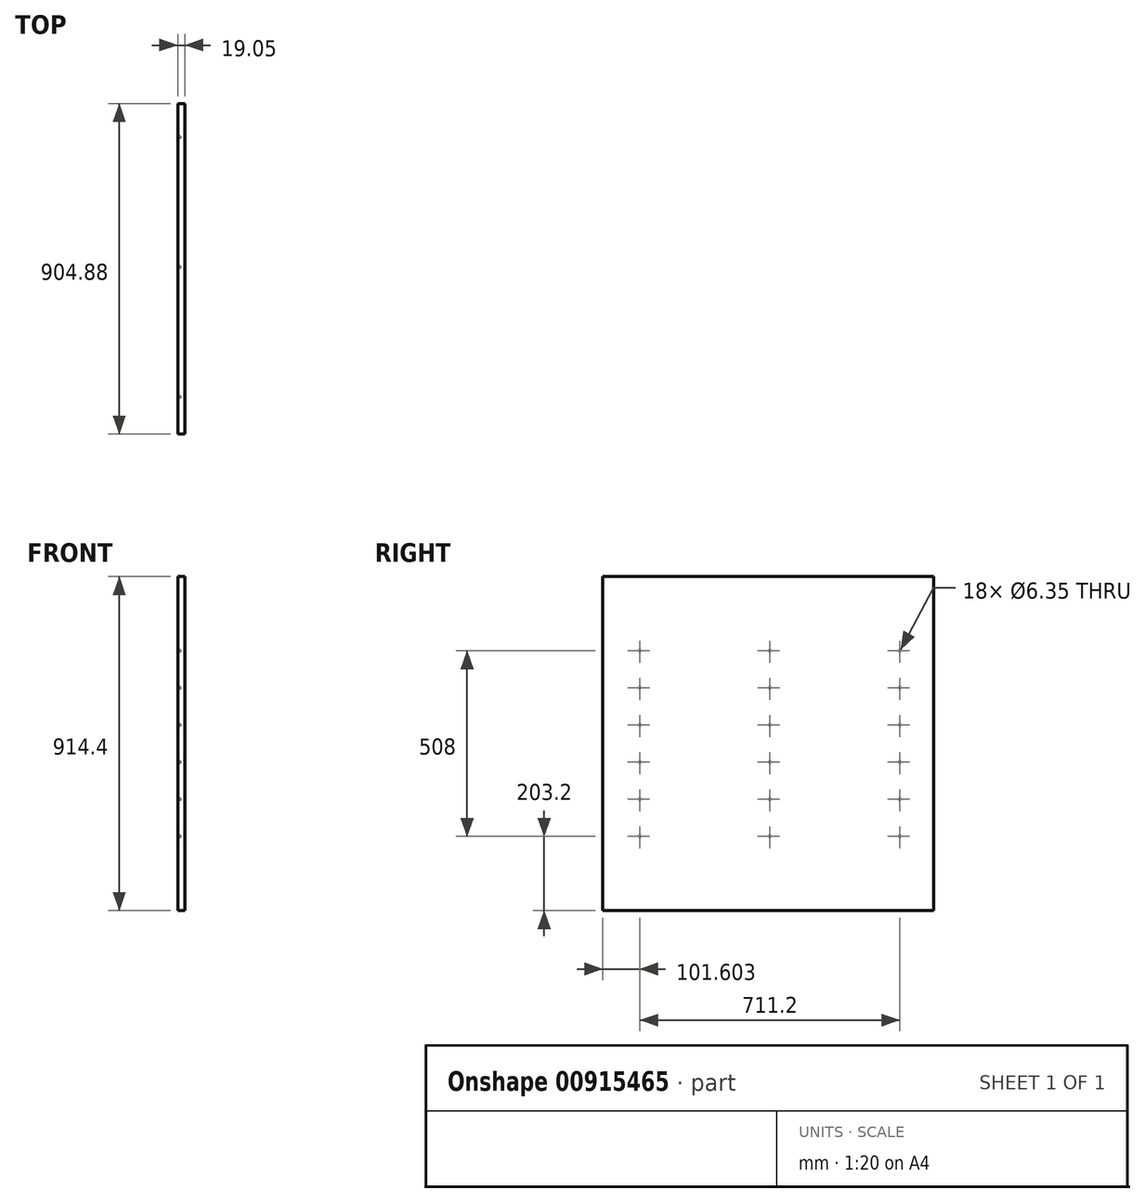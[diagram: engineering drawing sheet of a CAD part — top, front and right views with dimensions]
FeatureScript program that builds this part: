
annotation { "Feature Type Name" : "Feature", "Feature Type Description" : "" }
export const myFeature = defineFeature(function(context is Context, id is Id, definition is map)
    precondition{}
    {
        {
            var Q0;
            Q0=qCreatedBy(makeId("Right.planeOp"),FACE);
            var sketch = newSketch(context, id + "F0", { "sketchPlane" : qUnion([Q0])});
            skLineSegment(sketch, "E0.bottom", {"start": v(452.44, 457.2) * mm, "end": v(-452.44, 457.2) * mm});
            skLineSegment(sketch, "E0.top", {"start": v(452.44, -457.2) * mm, "end": v(-452.44, -457.2) * mm});
            skLineSegment(sketch, "E0.left", {"start": v(452.44, 457.2) * mm, "end": v(452.44, -457.2) * mm});
            skLineSegment(sketch, "E0.right", {"start": v(-452.44, 457.2) * mm, "end": v(-452.44, -457.2) * mm});
            skPoint(sketch, "E0.middle", {"position": v(0, 0) * mm});
            skSolve(sketch);
        }
        {
            var Q0;
            Q0=makeQuery(id+"F0.imprint","IMPRINT",FACE,{"disambiguationData":[TD([[makeQuery(id+"F0.imprint","IMPRINT",EDGE,{"derivedFrom":sQuery(id+"F0.wireOp",EDGE,"E0.bottom")}),1.0]])]});
            extrude(context, id + "F1", {"entities" : qUnion([Q0]), "depth" : 19.05 * mm, "offsetDistance" : 25.4 * mm});
        }
        {
            var Q0;
            Q0=makeQuery(id+"F1.opExtrude","CAP_FACE",FACE,{"disambiguationData":[OSD([sQuery(id+"F0.wireOp",EDGE,"E0.bottom"),sQuery(id+"F0.wireOp",EDGE,"E0.top"),sQuery(id+"F0.wireOp",EDGE,"E0.left"),sQuery(id+"F0.wireOp",EDGE,"E0.right")])],"isStart":true});
            var sketch = newSketch(context, id + "F2", { "sketchPlane" : qUnion([Q0])});
            skPoint(sketch, "E1", {"position": v(350.84, 254) * mm});
            skPoint(sketch, "E2.0.1.0", {"position": v(350.84, 152.4) * mm});
            skPoint(sketch, "E2.0.2.0", {"position": v(350.84, 50.8) * mm});
            skPoint(sketch, "E2.0.3.0", {"position": v(350.84, -50.8) * mm});
            skPoint(sketch, "E2.0.4.0", {"position": v(350.84, -152.4) * mm});
            skPoint(sketch, "E2.0.5.0", {"position": v(350.84, -254) * mm});
            skPoint(sketch, "E2.1.0.0", {"position": v(-4.76, 254) * mm});
            skPoint(sketch, "E2.1.1.0", {"position": v(-4.76, 152.4) * mm});
            skPoint(sketch, "E2.1.2.0", {"position": v(-4.76, 50.8) * mm});
            skPoint(sketch, "E2.1.3.0", {"position": v(-4.76, -50.8) * mm});
            skPoint(sketch, "E2.1.4.0", {"position": v(-4.76, -152.4) * mm});
            skPoint(sketch, "E2.1.5.0", {"position": v(-4.76, -254) * mm});
            skPoint(sketch, "E2.2.0.0", {"position": v(-360.36, 254) * mm});
            skPoint(sketch, "E2.2.1.0", {"position": v(-360.36, 152.4) * mm});
            skPoint(sketch, "E2.2.2.0", {"position": v(-360.36, 50.8) * mm});
            skPoint(sketch, "E2.2.3.0", {"position": v(-360.36, -50.8) * mm});
            skPoint(sketch, "E2.2.4.0", {"position": v(-360.36, -152.4) * mm});
            skPoint(sketch, "E2.2.5.0", {"position": v(-360.36, -254) * mm});
            skLineSegment(sketch, "E2.direction1", {"start": v(350.84, 254) * mm, "end": v(-4.76, 254) * mm, "construction": true});
            skLineSegment(sketch, "E2.direction2", {"start": v(350.84, 254) * mm, "end": v(350.84, 152.4) * mm, "construction": true});
            skSolve(sketch);
        }
        {
            var Q0;
            Q0=sQuery(id+"F2.wireOp",VERTEX,"E2.2.1.0");
            var Q1;
            Q1=sQuery(id+"F2.wireOp",VERTEX,"E2.0.1.0");
            var Q2;
            Q2=sQuery(id+"F2.wireOp",VERTEX,"E2.1.1.0");
            var Q3;
            Q3=sQuery(id+"F2.wireOp",VERTEX,"E2.2.5.0");
            var Q4;
            Q4=sQuery(id+"F2.wireOp",VERTEX,"E2.2.3.0");
            var Q5;
            Q5=sQuery(id+"F2.wireOp",VERTEX,"E2.1.2.0");
            var Q6;
            Q6=sQuery(id+"F2.wireOp",VERTEX,"E1");
            var Q7;
            Q7=sQuery(id+"F2.wireOp",VERTEX,"E2.0.4.0");
            var Q8;
            Q8=sQuery(id+"F2.wireOp",VERTEX,"E2.0.2.0");
            var Q9;
            Q9=sQuery(id+"F2.wireOp",VERTEX,"E2.direction1.end");
            var Q10;
            Q10=sQuery(id+"F2.wireOp",VERTEX,"E2.1.3.0");
            var Q11;
            Q11=sQuery(id+"F2.wireOp",VERTEX,"E2.2.2.0");
            var Q12;
            Q12=sQuery(id+"F2.wireOp",VERTEX,"E2.2.0.0");
            var Q13;
            Q13=sQuery(id+"F2.wireOp",VERTEX,"E2.0.5.0");
            var Q14;
            Q14=sQuery(id+"F2.wireOp",VERTEX,"E2.1.5.0");
            var Q15;
            Q15=sQuery(id+"F2.wireOp",VERTEX,"E2.1.4.0");
            var Q16;
            Q16=sQuery(id+"F2.wireOp",VERTEX,"E2.0.3.0");
            var Q17;
            Q17=sQuery(id+"F2.wireOp",VERTEX,"E2.2.4.0");
            var Q18;
            Q18=makeQuery(id+"F1.opExtrude","SWEPT_BODY",BODY,{"disambiguationData":[OSD([sQuery(id+"F0.wireOp",EDGE,"E0.bottom"),sQuery(id+"F0.wireOp",EDGE,"E0.top"),sQuery(id+"F0.wireOp",EDGE,"E0.left"),sQuery(id+"F0.wireOp",EDGE,"E0.right")])]});
            hole(context, id + "F3", {"style" : HoleStyle.SIMPLE, "endStyle" : HoleEndStyle.BLIND, "holeDiameter" : 6.35 * mm, "majorDiameter" : 6.35 * mm, "holeDepth" : 6.35 * mm, "isTappedThrough" : true, "tappedDepth" : 12.7 * mm, "tapClearance" : 3, "startFromSketch" : true, "locations" : qUnion([Q0, Q1, Q2, Q3, Q4, Q5, Q6, Q7, Q8, Q9, Q10, Q11, Q12, Q13, Q14, Q15, Q16, Q17]), "scope" : qUnion([Q18])});
        }
    });
